# Revit family: Legrand_Transformateur_triphasé_à_pertes_réduites
name_source: partatom
category: Installations électriques
revit_build: Autodesk Revit 2018 (Build: 20170223_1515(x64)
units: mm (PartAtom-declared; Revit-internal decimal feet)

## family parameters
Basée sur le plan de construction = Non
Conserver l'orientation des annotations = Non
Cote de connecteur circulaire = Utiliser le diamètre
Couper avec des vides une fois chargée = Non
Numéro OmniClass = 23.80.00.00
Partagée = Non
Point de calcul de pièce = Non
Titre OmniClass = Electric Power and Lighting
Toujours verticalement = Oui
Type d'élément = Normal

## types (5) — shared parameters
Conditions Générale d'Utilisation = https://export.legrand.com
Fabricant = Legrand
Modèle = Transformateurs d'isolement triphasés
Tension primaire = 400 V en Δ
Tension secondaire = 400 V en Y +N
URL = www.legrand.com

## per-type parameters (varying)
| type | 142860 | 142861 | 142862, 142863 | 142864 | Poids | Section câble primaire | Section câble secondaire | Ucc (%) | diamètre de fixation | dimension A | dimension B | dimension C | fixation F | fixation G | perte totale max | perte à vide | puissance |
| Transformateur triphasé à pertes réduites 142860 | Oui | Non | Non | Non | 243.00 kg | 35 mm² | 35 mm² | 3.5 | 12 mm  [stored 0.0393701 ft] | 530 mm  [stored 1.73885 ft] | 560 mm  [stored 1.83727 ft] | 460 mm  [stored 1.50919 ft] | 320 mm  [stored 1.04987 ft] | 430 mm  [stored 1.41076 ft] | 1413 W | 213 W | 50 kVA |
| Transformateur triphasé à pertes réduites 142861 | Non | Oui | Non | Non | 287.00 kg | 35 mm² | 35 mm² | 3.0 | 12 mm  [stored 0.0393701 ft] | 530 mm  [stored 1.73885 ft] | 560 mm  [stored 1.83727 ft] | 540 mm  [stored 1.77165 ft] | 320 mm  [stored 1.04987 ft] | 510 mm  [stored 1.67323 ft] | 1598 W | 268 W | 63 kVA |
| Transformateur triphasé à pertes réduites 142862 | Non | Non | Oui | Non | 363.00 kg | 70 mm² | 70 mm² | 3.2 | 16 mm  [stored 0.0524934 ft] | 670 mm  [stored 2.19816 ft] | 700 mm  [stored 2.29659 ft] | 610 mm  [stored 2.00131 ft] | 400 mm  [stored 1.31234 ft] | 580 mm  [stored 1.90289 ft] | 2035 W | 361 W | 80 kVA |
| Transformateur triphasé à pertes réduites 142863 | Non | Non | Oui | Non | 417.00 kg | 120 mm² | 70 mm² | 3.0 | 16 mm  [stored 0.0524934 ft] | 670 mm  [stored 2.19816 ft] | 700 mm  [stored 2.29659 ft] | 610 mm  [stored 2.00131 ft] | 400 mm  [stored 1.31234 ft] | 580 mm  [stored 1.90289 ft] | 2437 W | 424 W | 100 kVA |
| Transformateur triphasé à pertes réduites 142864 | Non | Non | Non | Oui | 551.00 kg | 120 mm² | 120 mm² | 3.1 | 16 mm  [stored 0.0524934 ft] | 820 mm  [stored 2.69029 ft] | 940 mm  [stored 3.08399 ft] | 880 mm  [stored 2.88714 ft] | 500 mm  [stored 1.64042 ft] | 820 mm  [stored 2.69029 ft] | 3229 W | 518 W | 125 kVA |

note: [stored X ft] marks values corroborated as IEEE doubles in the binary element streams (Revit-internal decimal feet)
